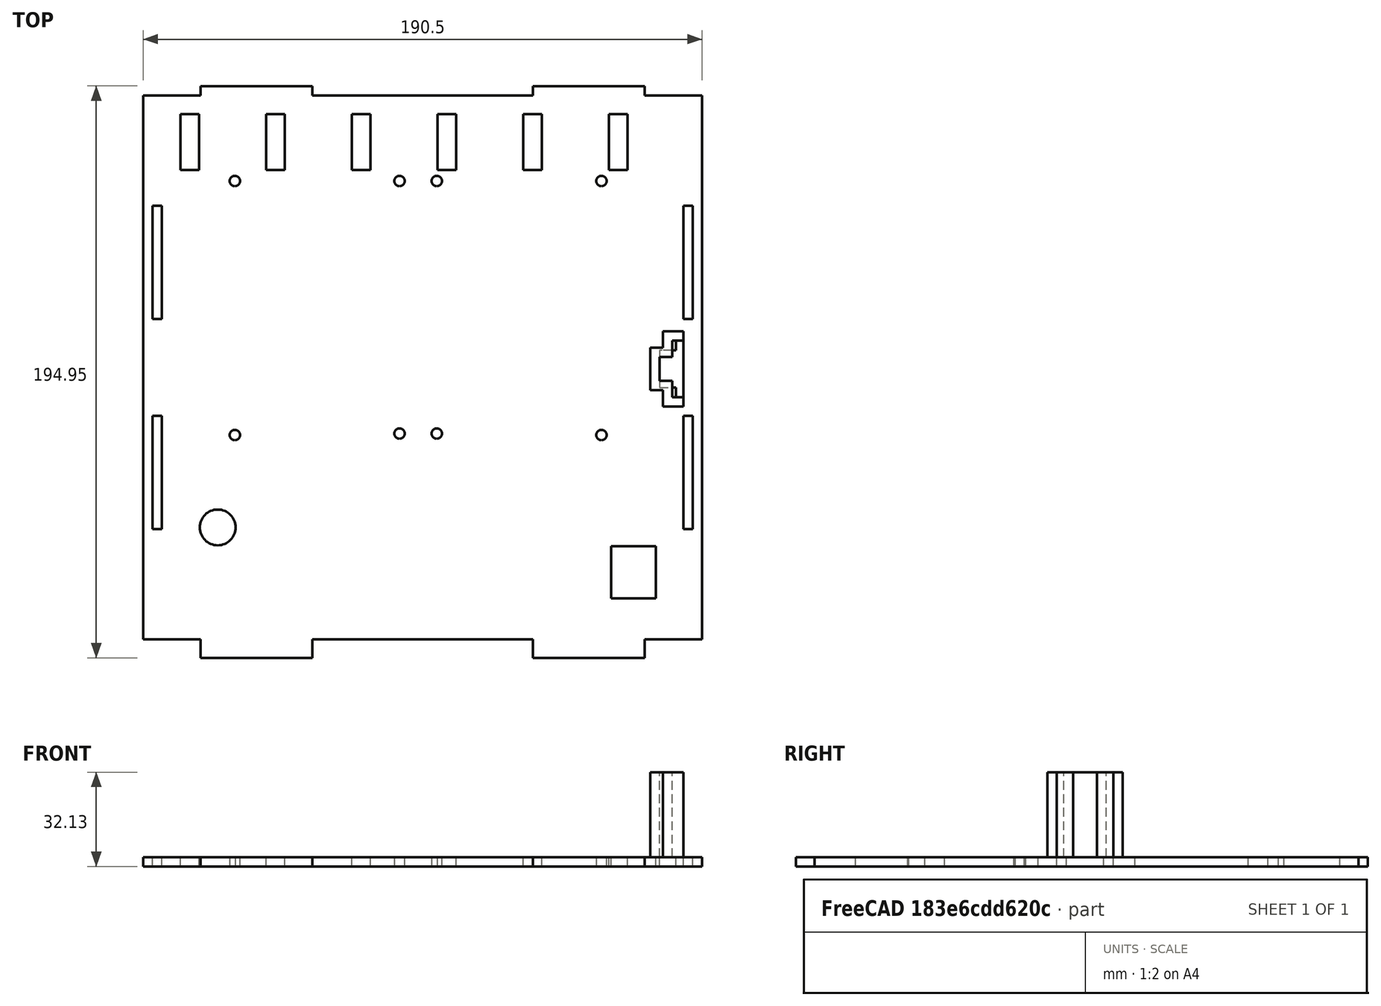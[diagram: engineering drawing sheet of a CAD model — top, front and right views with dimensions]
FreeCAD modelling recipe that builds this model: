
FCSTD DOCUMENT  (FreeCAD 0.18R4 (GitTag))
Label: bpr68k
License: All rights reserved
LicenseURL: http://en.wikipedia.org/wiki/All_rights_reserved
objects: Sketcher::SketchObject×2, PartDesign::Pad×2, PartDesign::Body×1, App::Part×1, Mesh::Feature×1
note: 7 computed .brp shape members not serialized (recipe doc carries the construction recipe); baked Part::Feature solids carry a one-line shape summary decoded from their .brp

FEATURE [Sketcher::SketchObject] Sketch
  MapMode = 2
  Support = -> [Sketch]
  sketch-geometry (81):
    g0: LineSegment StartX=-132.842 StartY=92.71 StartZ=0 EndX=-113.284 EndY=92.71 EndZ=0
    g1: LineSegment StartX=-113.284 StartY=92.71 StartZ=0 EndX=-113.284 EndY=95.885 EndZ=0
    g2: LineSegment StartX=-113.284 StartY=95.885 StartZ=0 EndX=-75.184 EndY=95.885 EndZ=0
    g3: LineSegment StartX=-75.184 StartY=95.885 StartZ=0 EndX=-75.184 EndY=92.71 EndZ=0
    g4: LineSegment StartX=-75.184 StartY=92.71 StartZ=0 EndX=0 EndY=92.71 EndZ=0
    g5: LineSegment StartX=0 StartY=92.71 StartZ=0 EndX=0 EndY=95.885 EndZ=0
    g6: LineSegment StartX=0 StartY=95.885 StartZ=0 EndX=38.1 EndY=95.885 EndZ=0
    g7: LineSegment StartX=38.1 StartY=95.885 StartZ=0 EndX=38.1 EndY=92.71 EndZ=0
    g8: LineSegment StartX=38.1 StartY=92.71 StartZ=0 EndX=57.658 EndY=92.71 EndZ=0
    g9: LineSegment StartX=57.658 StartY=92.71 StartZ=0 EndX=57.658 EndY=-92.71 EndZ=0
    g10: LineSegment StartX=57.658 StartY=-92.71 StartZ=0 EndX=38.1 EndY=-92.71 EndZ=0
    g11: LineSegment StartX=38.1 StartY=-92.71 StartZ=0 EndX=38.1 EndY=-99.06 EndZ=0
    g12: LineSegment StartX=38.1 StartY=-99.06 StartZ=0 EndX=-7.1e-15 EndY=-99.06 EndZ=0
    g13: LineSegment StartX=-7.1e-15 StartY=-99.06 StartZ=0 EndX=-4.2e-15 EndY=-92.71 EndZ=0
    g14: LineSegment StartX=-4.2e-15 StartY=-92.71 StartZ=0 EndX=-75.184 EndY=-92.71 EndZ=0
    g15: LineSegment StartX=-75.184 StartY=-92.71 StartZ=0 EndX=-75.184 EndY=-99.06 EndZ=0
    g16: LineSegment StartX=-75.184 StartY=-99.06 StartZ=0 EndX=-113.284 EndY=-99.06 EndZ=0
    g17: LineSegment StartX=-113.284 StartY=-99.06 StartZ=0 EndX=-113.284 EndY=-92.71 EndZ=0
    g18: LineSegment StartX=-113.284 StartY=-92.71 StartZ=0 EndX=-132.842 EndY=-92.71 EndZ=0
    g19: LineSegment StartX=-132.842 StartY=-92.71 StartZ=0 EndX=-132.842 EndY=92.71 EndZ=0
    g20: LineSegment StartX=-129.718 StartY=55.118 StartZ=0 EndX=-126.441 EndY=55.118 EndZ=0
    g21: LineSegment StartX=-126.441 StartY=55.118 StartZ=0 EndX=-126.441 EndY=16.51 EndZ=0
    g22: LineSegment StartX=-126.441 StartY=16.51 StartZ=0 EndX=-129.718 EndY=16.51 EndZ=0
    g23: LineSegment StartX=-129.718 StartY=16.51 StartZ=0 EndX=-129.718 EndY=55.118 EndZ=0
    g24: LineSegment StartX=51.2572 StartY=55.118 StartZ=0 EndX=54.5338 EndY=55.118 EndZ=0
    g25: LineSegment StartX=54.5338 StartY=55.118 StartZ=0 EndX=54.5338 EndY=16.51 EndZ=0
    g26: LineSegment StartX=54.5338 StartY=16.51 StartZ=0 EndX=51.2572 EndY=16.51 EndZ=0
    g27: LineSegment StartX=51.2572 StartY=16.51 StartZ=0 EndX=51.2572 EndY=55.118 EndZ=0
    g28: LineSegment StartX=51.2572 StartY=-16.51 StartZ=0 EndX=54.5338 EndY=-16.51 EndZ=0
    g29: LineSegment StartX=54.5338 StartY=-16.51 StartZ=0 EndX=54.5338 EndY=-55.118 EndZ=0
    g30: LineSegment StartX=54.5338 StartY=-55.118 StartZ=0 EndX=51.2572 EndY=-55.118 EndZ=0
    g31: LineSegment StartX=51.2572 StartY=-55.118 StartZ=0 EndX=51.2572 EndY=-16.51 EndZ=0
    g32: LineSegment StartX=-129.718 StartY=-16.51 StartZ=0 EndX=-126.441 EndY=-16.51 EndZ=0
    g33: LineSegment StartX=-126.441 StartY=-16.51 StartZ=0 EndX=-126.441 EndY=-55.118 EndZ=0
    g34: LineSegment StartX=-126.441 StartY=-55.118 StartZ=0 EndX=-129.718 EndY=-55.118 EndZ=0
    g35: LineSegment StartX=-129.718 StartY=-55.118 StartZ=0 EndX=-129.718 EndY=-16.51 EndZ=0
    g36: Circle CenterX=-107.442 CenterY=-54.61 CenterZ=0 NormalX=0 NormalY=0 NormalZ=1 AngleXU=0 Radius=6.096
    g37: LineSegment StartX=-120.142 StartY=86.36 StartZ=0 EndX=-113.792 EndY=86.36 EndZ=0
    g38: LineSegment StartX=-113.792 StartY=86.36 StartZ=0 EndX=-113.792 EndY=67.31 EndZ=0
    g39: LineSegment StartX=-113.792 StartY=67.31 StartZ=0 EndX=-120.142 EndY=67.31 EndZ=0
    g40: LineSegment StartX=-120.142 StartY=67.31 StartZ=0 EndX=-120.142 EndY=86.36 EndZ=0
    g41: LineSegment StartX=-84.582 StartY=86.36 StartZ=0 EndX=-90.932 EndY=86.36 EndZ=0
    g42: LineSegment StartX=-90.932 StartY=86.36 StartZ=0 EndX=-90.932 EndY=67.31 EndZ=0
    g43: LineSegment StartX=-90.932 StartY=67.31 StartZ=0 EndX=-84.582 EndY=67.31 EndZ=0
    g44: LineSegment StartX=-84.582 StartY=67.31 StartZ=0 EndX=-84.582 EndY=86.36 EndZ=0
    g45: LineSegment StartX=-61.722 StartY=86.36 StartZ=0 EndX=-55.372 EndY=86.36 EndZ=0
    g46: LineSegment StartX=-55.372 StartY=86.36 StartZ=0 EndX=-55.372 EndY=67.31 EndZ=0
    g47: LineSegment StartX=-55.372 StartY=67.31 StartZ=0 EndX=-61.722 EndY=67.31 EndZ=0
    g48: LineSegment StartX=-61.722 StartY=67.31 StartZ=0 EndX=-61.722 EndY=86.36 EndZ=0
    g49: LineSegment StartX=-32.512 StartY=86.36 StartZ=0 EndX=-26.162 EndY=86.36 EndZ=0
    g50: LineSegment StartX=-26.162 StartY=86.36 StartZ=0 EndX=-26.162 EndY=67.31 EndZ=0
    g51: LineSegment StartX=-26.162 StartY=67.31 StartZ=0 EndX=-32.512 EndY=67.31 EndZ=0
    g52: LineSegment StartX=-32.512 StartY=67.31 StartZ=0 EndX=-32.512 EndY=86.36 EndZ=0
    g53: LineSegment StartX=-3.302 StartY=86.36 StartZ=0 EndX=3.048 EndY=86.36 EndZ=0
    g54: LineSegment StartX=3.048 StartY=86.36 StartZ=0 EndX=3.048 EndY=67.31 EndZ=0
    g55: LineSegment StartX=3.048 StartY=67.31 StartZ=0 EndX=-3.302 EndY=67.31 EndZ=0
    g56: LineSegment StartX=-3.302 StartY=67.31 StartZ=0 EndX=-3.302 EndY=86.36 EndZ=0
    g57: LineSegment StartX=25.908 StartY=86.36 StartZ=0 EndX=32.258 EndY=86.36 EndZ=0
    g58: LineSegment StartX=32.258 StartY=86.36 StartZ=0 EndX=32.258 EndY=67.31 EndZ=0
    g59: LineSegment StartX=32.258 StartY=67.31 StartZ=0 EndX=25.908 EndY=67.31 EndZ=0
    g60: LineSegment StartX=25.908 StartY=67.31 StartZ=0 EndX=25.908 EndY=86.36 EndZ=0
    g61: Circle CenterX=-101.6 CenterY=63.5 CenterZ=0 NormalX=0 NormalY=0 NormalZ=1 AngleXU=0 Radius=1.778
    g62: Circle CenterX=-45.466 CenterY=63.5 CenterZ=0 NormalX=0 NormalY=0 NormalZ=1 AngleXU=0 Radius=1.778
    g63: Circle CenterX=-101.6 CenterY=-23.114 CenterZ=0 NormalX=0 NormalY=0 NormalZ=1 AngleXU=0 Radius=1.778
    g64: Circle CenterX=-45.466 CenterY=-22.606 CenterZ=0 NormalX=0 NormalY=0 NormalZ=1 AngleXU=0 Radius=1.778
    g65: Circle CenterX=-32.766 CenterY=63.5 CenterZ=0 NormalX=0 NormalY=0 NormalZ=1 AngleXU=0 Radius=1.778
    g66: Circle CenterX=23.368 CenterY=63.5 CenterZ=0 NormalX=0 NormalY=0 NormalZ=1 AngleXU=0 Radius=1.778
    g67: Circle CenterX=-32.766 CenterY=-22.606 CenterZ=0 NormalX=0 NormalY=0 NormalZ=1 AngleXU=0 Radius=1.778
    g68: Circle CenterX=23.368 CenterY=-23.114 CenterZ=0 NormalX=0 NormalY=0 NormalZ=1 AngleXU=0 Radius=1.778
    g69: LineSegment StartX=26.6192 StartY=-60.96 StartZ=0 EndX=41.8592 EndY=-60.96 EndZ=0
    g70: LineSegment StartX=41.8592 StartY=-60.96 StartZ=0 EndX=41.8592 EndY=-78.74 EndZ=0
    g71: LineSegment StartX=41.8592 StartY=-78.74 StartZ=0 EndX=26.6192 EndY=-78.74 EndZ=0
    g72: LineSegment StartX=26.6192 StartY=-78.74 StartZ=0 EndX=26.6192 EndY=-60.96 EndZ=0
    g73: LineSegment StartX=51.2572 StartY=9.144 StartZ=0 EndX=48.7172 EndY=9.144 EndZ=0
    g74: LineSegment StartX=48.7172 StartY=9.144 StartZ=0 EndX=48.7172 EndY=5.842 EndZ=0
    g75: LineSegment StartX=48.7172 StartY=5.842 StartZ=0 EndX=43.1292 EndY=5.842 EndZ=0
    g76: LineSegment StartX=43.1292 StartY=5.842 StartZ=0 EndX=43.1292 EndY=-6.858 EndZ=0
    g77: LineSegment StartX=43.1292 StartY=-6.858 StartZ=0 EndX=48.7172 EndY=-6.858 EndZ=0
    g78: LineSegment StartX=48.7172 StartY=-6.858 StartZ=0 EndX=48.7172 EndY=-10.16 EndZ=0
    g79: LineSegment StartX=48.7172 StartY=-10.16 StartZ=0 EndX=51.2572 EndY=-10.16 EndZ=0
    g80: LineSegment StartX=51.2572 StartY=-10.16 StartZ=0 EndX=51.2572 EndY=9.144 EndZ=0
  constraints (241):
    c: Horizontal(g0)
    c: Coincident(g0,g1)
    c: Vertical(g1)
    c: Coincident(g1,g2)
    c: Horizontal(g2)
    c: Coincident(g2,g3)
    c: Coincident(g3,g4)
    c: Horizontal(g4)
    c: Coincident(g4,g5)
    c: PointOnObject(g5,g-2)
    c: Vertical(g5)
    c: Coincident(g5,g6)
    c: Coincident(g6,g7)
    c: Coincident(g7,g8)
    c: Horizontal(g8)
    c: Coincident(g8,g9)
    c: Coincident(g9,g10)
    c: Horizontal(g10)
    c: Coincident(g10,g11)
    c: Vertical(g11)
    c: Coincident(g11,g12)
    c: Coincident(g12,g13)
    c: Coincident(g13,g14)
    c: Horizontal(g14)
    c: Coincident(g14,g15)
    c: Coincident(g15,g16)
    c: Horizontal(g16)
    c: Coincident(g16,g17)
    c: Coincident(g17,g18)
    c: Horizontal(g18)
    c: Coincident(g18,g19)
    c: Coincident(g19,g0)
    c: Symmetric(g0,g18,g-1)
    c: Symmetric(g8,g9,g-1)
    c: Equal(g9,g19)
    c: DistanceY(g9,g8) = 185.42
    c: Perpendicular(g3,g2)
    c: Perpendicular(g7,g6)
    c: Perpendicular(g13,g12)
    c: Perpendicular(g15,g14)
    c: Equal(g17,g15)
    c: Equal(g15,g13)
    c: Equal(g13,g11)
    c: Equal(g10,g18)
    c: Equal(g18,g0)
    c: Equal(g0,g8)
    c: Equal(g7,g5)
    c: Equal(g5,g3)
    c: Equal(g3,g1)
    c: DistanceX(g10,g9) = 19.558
    c: Equal(g12,g16)
    c: Equal(g16,g2)
    c: Equal(g2,g6)
    c: Equal(g4,g14)
    c: DistanceX(g12,g11) = 38.1
    c: DistanceX(g3,g4) = 75.184
    c: DistanceY(g7,g6) = 3.175
    c: DistanceY(g16,g17) = 6.35
    c: Coincident(g20,g21)
    c: Coincident(g21,g22)
    c: Coincident(g22,g23)
    c: Coincident(g23,g20)
    c: Horizontal(g20)
    c: Horizontal(g22)
    c: Vertical(g21)
    c: Vertical(g23)
    c: DistanceY(g20,g0) = 37.592
    c: DistanceX(g0,g20) = 3.1242
    c: Coincident(g24,g25)
    c: Coincident(g25,g26)
    c: Coincident(g26,g27)
    c: Coincident(g27,g24)
    c: Horizontal(g24)
    c: Horizontal(g26)
    c: Vertical(g25)
    c: Vertical(g27)
    c: DistanceY(g24,g8) = 37.592
    c: DistanceX(g24,g8) = 3.1242
    c: Coincident(g28,g29)
    c: Coincident(g29,g30)
    c: Coincident(g30,g31)
    c: Coincident(g31,g28)
    c: Horizontal(g28)
    c: Horizontal(g30)
    c: Vertical(g29)
    c: Vertical(g31)
    c: DistanceY(g9,g29) = 37.592
    c: DistanceX(g29,g9) = 3.1242
    c: Coincident(g32,g33)
    c: Coincident(g33,g34)
    c: Coincident(g34,g35)
    c: Coincident(g35,g32)
    c: Horizontal(g32)
    c: Horizontal(g34)
    c: Vertical(g33)
    c: Vertical(g35)
    c: DistanceY(g18,g34) = 37.592
    c: DistanceX(g18,g34) = 3.1242
    c: Equal(g33,g31)
    c: Equal(g31,g27)
    c: Equal(g27,g21)
    c: DistanceY(g33,g32) = 38.608
    c: Equal(g28,g26)
    c: Equal(g26,g22)
    c: Equal(g22,g32)
    c: DistanceX(g28,g28) = 3.2766
    c: Diameter(g36) = 12.192
    c: DistanceY(g9,g36) = 38.1
    c: Coincident(g37,g38)
    c: Coincident(g38,g39)
    c: Coincident(g39,g40)
    c: Coincident(g40,g37)
    c: Horizontal(g37)
    c: Horizontal(g39)
    c: Vertical(g38)
    c: Vertical(g40)
    c: Coincident(g41,g42)
    c: Coincident(g42,g43)
    c: Coincident(g43,g44)
    c: Coincident(g44,g41)
    c: Horizontal(g41)
    c: Horizontal(g43)
    c: Vertical(g42)
    c: Vertical(g44)
    c: Coincident(g45,g46)
    c: Coincident(g46,g47)
    c: Coincident(g47,g48)
    c: Coincident(g48,g45)
    c: Horizontal(g45)
    c: Horizontal(g47)
    c: Vertical(g46)
    c: Vertical(g48)
    c: Coincident(g49,g50)
    c: Coincident(g50,g51)
    c: Coincident(g51,g52)
    c: Coincident(g52,g49)
    c: Horizontal(g49)
    c: Horizontal(g51)
    c: Vertical(g50)
    c: Vertical(g52)
    c: Coincident(g53,g54)
    c: Coincident(g54,g55)
    c: Coincident(g55,g56)
    c: Coincident(g56,g53)
    c: Horizontal(g53)
    c: Horizontal(g55)
    c: Vertical(g54)
    c: Vertical(g56)
    c: Coincident(g57,g58)
    c: Coincident(g58,g59)
    c: Coincident(g59,g60)
    c: Coincident(g60,g57)
    c: Horizontal(g57)
    c: Horizontal(g59)
    c: Vertical(g58)
    c: Vertical(g60)
    c: DistanceX(g57,g8) = 31.75
    c: DistanceY(g57,g8) = 6.35
    c: DistanceX(g49,g53) = 29.21
    c: DistanceX(g53,g57) = 29.21
    c: DistanceX(g45,g49) = 29.21
    c: DistanceX(g41,g45) = 29.21
    c: DistanceX(g37,g41) = 29.21
    c: Equal(g57,g53)
    c: Equal(g53,g49)
    c: Equal(g49,g45)
    c: Equal(g45,g41)
    c: Equal(g41,g37)
    c: DistanceX(g57,g57) = 6.35
    c: DistanceY(g53,g57) = 0
    c: DistanceY(g49,g57) = 0
    c: DistanceY(g45,g57) = 0
    c: DistanceY(g41,g57) = 0
    c: DistanceY(g37,g57) = 0
    c: Equal(g60,g56)
    c: Equal(g56,g52)
    c: Equal(g52,g48)
    c: Equal(g48,g42)
    c: Equal(g42,g40)
    c: DistanceY(g59,g57) = 19.05
    c: Diameter(g61) = 3.556
    c: Equal(g61,g68)
    c: Equal(g61,g62)
    c: Equal(g62,g63)
    c: Equal(g63,g64)
    c: Equal(g64,g65)
    c: Equal(g65,g66)
    c: Equal(g66,g67)
    c: DistanceY(g-1,g61) = 63.5
    c: DistanceY(g-1,g62) = 63.5
    c: DistanceY(g-1,g65) = 63.5
    c: DistanceY(g-1,g66) = 63.5
    c: DistanceX(g61,g62) = 56.134
    c: DistanceX(g65,g66) = 56.134
    c: DistanceX(g63,g64) = 56.134
    c: DistanceY(g63,g61) = 86.614
    c: DistanceY(g64,g62) = 86.106
    c: DistanceX(g61,g63) = 0
    c: DistanceY(g67,g65) = 86.106
    c: DistanceY(g68,g66) = 86.614
    c: DistanceX(g67,g68) = 56.134
    c: DistanceX(g65,g67) = 0
    c: DistanceX(g61,g-1) = 101.6
    c: DistanceX(g62,g65) = 12.7
    c: Coincident(g69,g70)
    c: Coincident(g70,g71)
    c: Coincident(g71,g72)
    c: Coincident(g72,g69)
    c: Horizontal(g69)
    c: Horizontal(g71)
    c: Vertical(g70)
    c: Vertical(g72)
    c: DistanceY(g70,g69) = 17.78
    c: DistanceX(g69,g69) = 15.24
    c: DistanceY(g17,g71) = 13.97
    c: DistanceX(g69,g30) = 9.398
    c: DistanceX(g18,g36) = 25.4
    c: Horizontal(g73)
    c: Coincident(g73,g74)
    c: Vertical(g74)
    c: Coincident(g74,g75)
    c: Horizontal(g75)
    c: Coincident(g75,g76)
    c: Vertical(g76)
    c: Coincident(g76,g77)
    c: Horizontal(g77)
    c: Coincident(g77,g78)
    c: Vertical(g78)
    c: Coincident(g78,g79)
    c: Horizontal(g79)
    c: Coincident(g79,g80)
    c: Coincident(g80,g73)
    c: Equal(g79,g73)
    c: Equal(g77,g75)
    c: Equal(g74,g78)
    c: DistanceY(g76,g75) = 12.7
    c: DistanceY(g79,g73) = 19.304
    c: DistanceX(g73,g73) = 2.54
    c: DistanceX(g75,g74) = 5.588
    c: DistanceY(g69,g78) = 50.8
    c: DistanceX(g73,g26) = 0
FEATURE [Sketcher::SketchObject] Sketch001
  MapMode = 5
  Placement = pos=(0,0,3.175) rot=(0,0,1;0rad)
  sketch-geometry (16):
    g0: LineSegment StartX=51.2572 StartY=9.144 StartZ=0 EndX=51.2572 EndY=12.319 EndZ=0
    g1: LineSegment StartX=51.2572 StartY=12.319 StartZ=0 EndX=44.2722 EndY=12.319 EndZ=0
    g2: LineSegment StartX=44.2722 StartY=12.319 StartZ=0 EndX=44.2722 EndY=6.731 EndZ=0
    g3: LineSegment StartX=44.2722 StartY=6.731 StartZ=0 EndX=39.9542 EndY=6.731 EndZ=0
    g4: LineSegment StartX=39.9542 StartY=6.731 StartZ=0 EndX=39.9542 EndY=-7.747 EndZ=0
    g5: LineSegment StartX=39.9542 StartY=-7.747 StartZ=0 EndX=44.2722 EndY=-7.747 EndZ=0
    g6: LineSegment StartX=44.2722 StartY=-7.747 StartZ=0 EndX=44.2722 EndY=-13.335 EndZ=0
    g7: LineSegment StartX=44.2722 StartY=-13.335 StartZ=0 EndX=51.2572 EndY=-13.335 EndZ=0
    g8: LineSegment StartX=51.2572 StartY=-13.335 StartZ=0 EndX=51.2572 EndY=-10.16 EndZ=0
    g9: LineSegment StartX=51.2572 StartY=-10.16 StartZ=0 EndX=47.4472 EndY=-10.16 EndZ=0
    g10: LineSegment StartX=47.4472 StartY=-10.16 StartZ=0 EndX=47.4472 EndY=-4.572 EndZ=0
    g11: LineSegment StartX=47.4472 StartY=-4.572 StartZ=0 EndX=43.1292 EndY=-4.572 EndZ=0
    g12: LineSegment StartX=43.1292 StartY=-4.572 StartZ=0 EndX=43.1292 EndY=3.556 EndZ=0
    g13: LineSegment StartX=43.1292 StartY=3.556 StartZ=0 EndX=47.4472 EndY=3.556 EndZ=0
    g14: LineSegment StartX=47.4472 StartY=3.556 StartZ=0 EndX=47.4472 EndY=9.144 EndZ=0
    g15: LineSegment StartX=47.4472 StartY=9.144 StartZ=0 EndX=51.2572 EndY=9.144 EndZ=0
  constraints (48):
    c: Coincident(g0,g1)
    c: Coincident(g1,g2)
    c: Vertical(g2)
    c: Coincident(g2,g3)
    c: Coincident(g3,g4)
    c: Vertical(g4)
    c: Coincident(g4,g5)
    c: Horizontal(g5)
    c: Coincident(g5,g6)
    c: Vertical(g6)
    c: Coincident(g6,g7)
    c: Horizontal(g7)
    c: Coincident(g7,g8)
    c: Coincident(g8,g9)
    c: Horizontal(g9)
    c: Coincident(g9,g10)
    c: Coincident(g10,g11)
    c: Coincident(g11,g12)
    c: Coincident(g12,g13)
    c: Horizontal(g13)
    c: Coincident(g13,g14)
    c: Coincident(g14,g15)
    c: Coincident(g15,g0)
    c: Horizontal(g15)
    c: Vertical(g8)
    c: Vertical(g0)
    c: Vertical(g14)
    c: Vertical(g10)
    c: Horizontal(g1)
    c: Horizontal(g3)
    c: Horizontal(g11)
    c: Equal(g2,g6)
    c: Equal(g14,g10)
    c: Equal(g1,g7)
    c: Equal(g15,g9)
    c: Equal(g11,g13)
    c: Equal(g5,g3)
    c: DistanceY(g7,g8) = 3.175
    c: Equal(g8,g0)
    c: DistanceX(g14,g0) = 3.81
    c: DistanceX(g11,g10) = 4.318
    c: DistanceY(g11,g12) = 8.128
    c: DistanceY(g13,g14) = 5.588
    c: DistanceY(g9,g-1) = 10.16
    c: DistanceX(g1,g0) = 6.985
    c: DistanceX(g3,g2) = 4.318
    c: DistanceY(g2,g1) = 5.588
    c: DistanceX(g-1,g0) = 51.2572
FEATURE [PartDesign::Pad] Pad001
  Length = 28.956
  Length2 = 99.9998
  Placement = pos=(0,0,3.175) rot=(0,0,1;0rad)
  Profile = -> Sketch001
  Type = 0
FEATURE [PartDesign::Pad] Pad
  BaseFeature = -> Pad001
  Length = 3.175
  Length2 = 99.9998
  Placement = pos=(0,0,3.175) rot=(0,0,1;0rad)
  Profile = -> Sketch
  Type = 0
FEATURE [PartDesign::Body] Body
  Group = -> [Sketch,Sketch001,Pad001,Pad]
  Origin = -> Origin001
  Tip = -> Pad
FEATURE [App::Part] Part
  Group = -> [Body]
  Origin = -> Origin
FEATURE [Mesh::Feature] Mesh  label="bpr68k"
